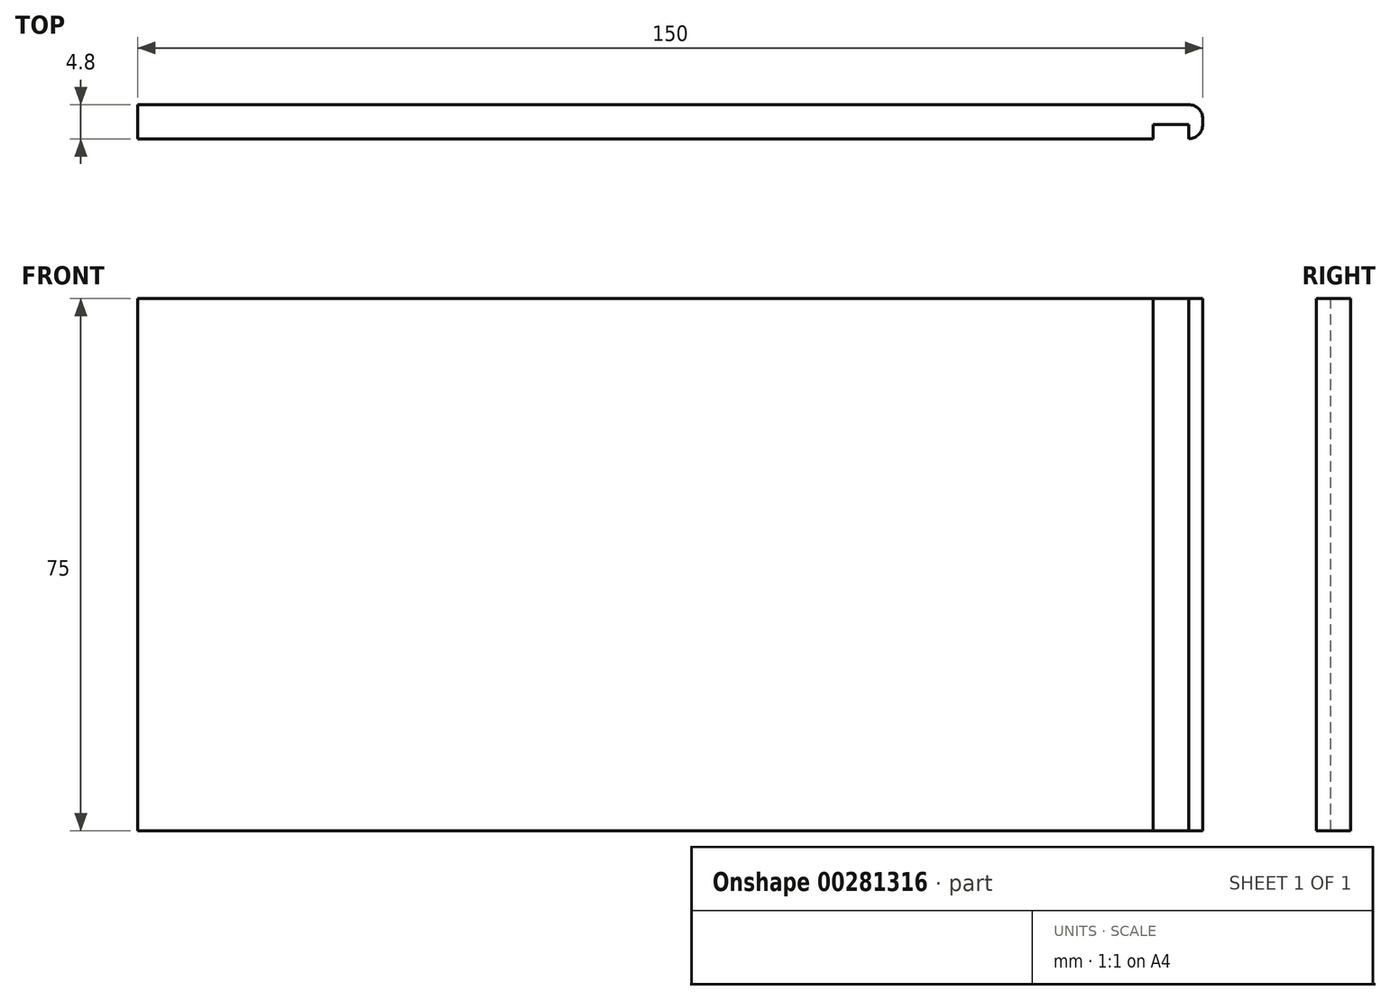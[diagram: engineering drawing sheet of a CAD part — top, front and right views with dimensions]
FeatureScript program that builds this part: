
annotation { "Feature Type Name" : "Feature", "Feature Type Description" : "" }
export const myFeature = defineFeature(function(context is Context, id is Id, definition is map)
    precondition{}
    {
        {
            var Q0;
            Q0=qCreatedBy(makeId("Front.planeOp"),FACE);
            var sketch = newSketch(context, id + "F0", { "sketchPlane" : qUnion([Q0])});
            skLineSegment(sketch, "E0.bottom", {"start": v(75, -37.5) * mm, "end": v(-75, -37.5) * mm});
            skLineSegment(sketch, "E0.top", {"start": v(75, 37.5) * mm, "end": v(-75, 37.5) * mm});
            skLineSegment(sketch, "E0.left", {"start": v(75, -37.5) * mm, "end": v(75, 37.5) * mm});
            skLineSegment(sketch, "E0.right", {"start": v(-75, -37.5) * mm, "end": v(-75, 37.5) * mm});
            skPoint(sketch, "E0.middle", {"position": v(0, 0) * mm});
            skSolve(sketch);
        }
        {
            var Q0;
            Q0=qSketchRegion(id+"F0",true);
            extrude(context, id + "F1", {"entities" : qUnion([Q0]), "depth" : 4.8 * mm});
        }
        {
            var Q0;
            Q0=makeQuery(id+"F1.opExtrude","CAP_FACE",FACE,{"disambiguationData":[OSD([sQuery(id+"F0.wireOp",EDGE,"E0.bottom"),sQuery(id+"F0.wireOp",EDGE,"E0.top"),sQuery(id+"F0.wireOp",EDGE,"E0.left"),sQuery(id+"F0.wireOp",EDGE,"E0.right")])],"isStart":false});
            var sketch = newSketch(context, id + "F2", { "sketchPlane" : qUnion([Q0])});
            skLineSegment(sketch, "E1.bottom", {"start": v(68, -37.5) * mm, "end": v(73, -37.5) * mm});
            skLineSegment(sketch, "E1.top", {"start": v(68, 37.5) * mm, "end": v(73, 37.5) * mm});
            skLineSegment(sketch, "E1.left", {"start": v(68, -37.5) * mm, "end": v(68, 37.5) * mm});
            skLineSegment(sketch, "E1.right", {"start": v(73, -37.5) * mm, "end": v(73, 37.5) * mm});
            skPoint(sketch, "E1.middle", {"position": v(70.5, 0) * mm});
            skSolve(sketch);
        }
        {
            var Q0;
            Q0=qSketchRegion(id+"F2",true);
            extrude(context, id + "F3", {"entities" : qUnion([Q0]), "operationType" : NewBodyOperationType.REMOVE, "oppositeDirection" : true, "depth" : 2 * mm});
        }
        {
            var Q0;
            Q0=makeQuery(id+"F1.opExtrude","CAP_EDGE",EDGE,{"disambiguationData":[OSD([sQuery(id+"F0.wireOp",EDGE,"E0.left")])],"isStart":true});
            var Q1;
            {var subQ0=sQuery(id+"F0.wireOp",EDGE,"E0.left");var subQ1=sQuery(id+"F0.wireOp",EDGE,"E0.top");var subQ3=makeQuery(id+"F1.opExtrude","CAP_EDGE",EDGE,{"disambiguationData":[OSD([subQ0])],"isStart":false});Q1=makeQuery(id+"F3.boolean.opBoolean","SPLIT",EDGE,{"disambiguationData":[TD([makeQuery(id+"F1.opExtrude","SWEPT_FACE",FACE,{"disambiguationData":[OSD([subQ1])]})])],"derivedFrom":subQ3});}
            fillet(context, id + "F4", {"entities" : qUnion([Q0, Q1]), "radius" : 2 * mm, "tangentPropagation" : true, "allowEdgeOverflow" : false});
        }
    });
